# Revit family: Dali Barstool Laminate
name_source: partatom
category: Arredi
revit_build: Autodesk Revit 2017 (Build: 20160225_1515(x64)
units: mm (PartAtom-declared; Revit-internal decimal feet)

## family parameters
Basato su piano di lavoro = No
Condiviso = No
Numero OmniClass = 23.40.20.00
Punto di calcolo locali = No
Sempre verticale = Sì
Taglio con vuoti quando caricato = No
Titolo OmniClass = General Furniture and Specialties

## types (1)
- Dali Barstool Laminate
    Abet laminate = Abet Standard finishes or COF
    Assistance = Call for assistance number: 336.941.3446
    Chair type = Side
    Codice assieme = E2020200
    Collection = Dali
    Commenti sul tipo = Ideal for Cafeteria, Church, Dining, Hospitality, Institutional, Office, University
    Depth = 21 mm
    Descrizione = Laminate seat Abet and legs tapered mixing metal with wood
    Height = 42 mm  [stored 0.137795 ft]
    Industry = Café, Restaurant, Bistro, Hotel, Club, College
    Manufacturer Country = USA
    Modello = Dali Barstool Laminate
    Products of collection = Dali Side Chair, Pad, Uph, Pronto, Laminate and Barstool Wood Veneer, Papped Seat, Upholstered, Pronto
    Produttore = Beaufurn
    Seat height = 30 mm  [stored 0.0984252 ft]
    URL = https://beaufurn.com
    Usage = Indoor
    Width = 21 mm
    Wood legs = Standard wood finishes or COF

note: [stored X ft] marks values corroborated as IEEE doubles in the binary element streams (Revit-internal decimal feet)
